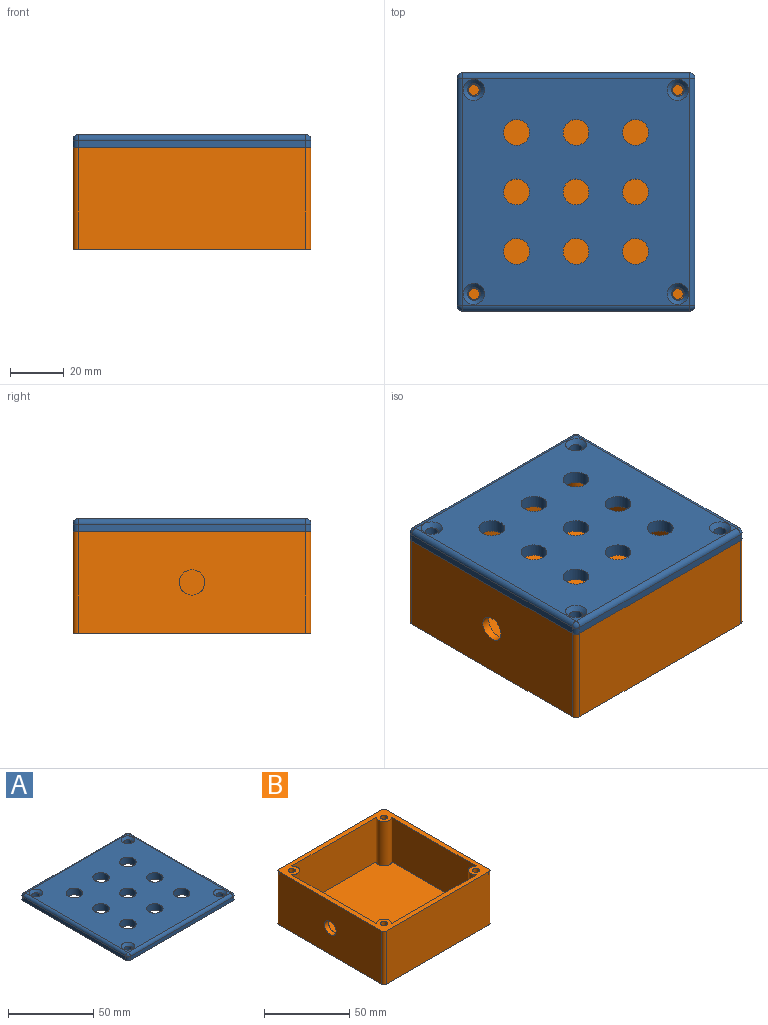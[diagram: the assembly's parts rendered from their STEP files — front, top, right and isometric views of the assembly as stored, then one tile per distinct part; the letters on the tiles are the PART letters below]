
ASSEMBLY  parts=2 mates=1
PART A: 35 faces, bbox 88.9x88.9x4.8 mm
  f0: plane 84.84x2.73mm, normal (1,0,0), area 231.6mm2, adj f18,f21,f27,f30
  f1: plane 84.84x2.73mm, normal (0,1,0), area 231.6mm2, adj f18,f24,f28,f30
  f2: plane 84.84x2.73mm, normal (-1,0,0), area 231.6mm2, adj f18,f19,f23,f24
  f3: cylinder r=2.38mm len=4.76mm, axis (0,0,-1), area 47.3mm2, adj f18,f31
  f4: cylinder r=2.38mm len=4.76mm, axis (0,0,-1), area 47.3mm2, adj f18,f33
  f5: cylinder r=2.38mm len=4.76mm, axis (0,0,-1), area 47.3mm2, adj f18,f34
  f6: cylinder r=4.83mm len=9.65mm, axis (0,0,-1), area 144.4mm2, adj f17,f18
  f7: cylinder r=4.83mm len=9.65mm, axis (0,0,-1), area 144.4mm2, adj f17,f18
  f8: cylinder r=4.83mm len=9.65mm, axis (0,0,-1), area 144.4mm2, adj f17,f18
  f9: cylinder r=4.83mm len=9.65mm, axis (0,0,-1), area 144.4mm2, adj f17,f18
  f10: cylinder r=4.83mm len=9.65mm, axis (0,0,-1), area 144.4mm2, adj f17,f18
  f11: cylinder r=4.83mm len=9.65mm, axis (0,0,-1), area 144.4mm2, adj f17,f18
  f12: cylinder r=4.83mm len=9.65mm, axis (0,0,-1), area 144.4mm2, adj f17,f18
  f13: cylinder r=4.83mm len=9.65mm, axis (0,0,-1), area 144.4mm2, adj f17,f18
  f14: cylinder r=4.83mm len=9.65mm, axis (0,0,-1), area 144.4mm2, adj f17,f18
  f15: plane 84.84x2.73mm, normal (0,-1,0), area 231.6mm2, adj f18,f19,f21,f22
  f16: cylinder r=2.38mm len=4.76mm, axis (0,0,-1), area 47.3mm2, adj f18,f32
  f17: plane 84.84x84.84mm, normal (0,0,1), area 6340.7mm2, adj f6,f7,f8,f9,f10,f11,f12,f13
  f18: plane 88.9x88.9mm, normal (0,0,-1), area 7169.9mm2, adj f0,f1,f2,f3,f4,f5,f6,f7
  f19: cylinder r=2.03mm len=2.73mm, axis (0,0,1), area 8.7mm2, adj f2,f15,f18,f20
  f20: sphere r=2.03mm, area 6.5mm2, adj f19,f22,f23
  f21: cylinder r=2.03mm len=2.73mm, axis (0,0,-1), area 8.7mm2, adj f0,f15,f18,f25
  f22: cylinder r=2.03mm len=84.84mm, axis (-1,0,0), area 270.8mm2, adj f15,f17,f20,f25
  f23: cylinder r=2.03mm len=84.84mm, axis (0,1,0), area 270.8mm2, adj f2,f17,f20,f26
  f24: cylinder r=2.03mm len=2.73mm, axis (0,0,-1), area 8.7mm2, adj f1,f2,f18,f26
  f25: sphere r=2.03mm, area 6.5mm2, adj f21,f22,f27
  f26: sphere r=2.03mm, area 6.5mm2, adj f23,f24,f28
  f27: cylinder r=2.03mm len=84.84mm, axis (0,-1,0), area 270.8mm2, adj f0,f17,f25,f29
  f28: cylinder r=2.03mm len=84.84mm, axis (1,0,0), area 270.8mm2, adj f1,f17,f26,f29
  f29: sphere r=2.03mm, area 6.5mm2, adj f27,f28,f30
  f30: cylinder r=2.03mm len=2.73mm, axis (0,0,1), area 8.7mm2, adj f0,f1,f18,f29
  f31: cone r=2.38mm half-angle=44.8deg, axis (0,0,1), area 45mm2, adj f3,f17
  f32: cone r=2.38mm half-angle=44.8deg, axis (0,0,1), area 45mm2, adj f16,f17
  f33: cone r=2.38mm half-angle=44.8deg, axis (0,0,1), area 45mm2, adj f4,f17
  f34: cone r=2.38mm half-angle=44.8deg, axis (0,0,1), area 45mm2, adj f5,f17
PART B: 28 faces, bbox 88.9x88.9x38.1 mm
  f0: plane 69.85x31.75mm, normal (0,1,0), area 2217.7mm2, adj f1,f15,f16,f18
  f1: cylinder r=4.49mm len=31.75mm, axis (0,0,-1), area 447.9mm2, adj f0,f2,f16,f18
  f2: plane 69.85x31.75mm, normal (1,0,0), area 2146.5mm2, adj f1,f3,f16,f18,f27
  f3: cylinder r=4.49mm len=31.75mm, axis (0,0,-1), area 447.9mm2, adj f2,f4,f16,f18
  f4: plane 69.85x31.75mm, normal (0,-1,0), area 2217.7mm2, adj f3,f5,f16,f18
  f5: cylinder r=4.49mm len=31.75mm, axis (0,0,-1), area 447.9mm2, adj f4,f6,f16,f18
  f6: plane 69.85x31.75mm, normal (-1,0,0), area 2217.7mm2, adj f5,f15,f16,f18
  f7: plane 84.84x38.1mm, normal (1,0,0), area 3232.3mm2, adj f16,f17,f23,f26
  f8: plane 84.84x38.1mm, normal (0,1,0), area 3232.3mm2, adj f16,f17,f23,f24
  f9: plane 84.84x38.1mm, normal (-1,0,0), area 3161mm2, adj f16,f17,f24,f25,f27
  f10: cylinder r=2.1mm len=31.75mm, axis (0,0,-1), area 418.7mm2, adj f16,f22
  f11: cylinder r=1.98mm len=31.75mm, axis (0,0,-1), area 395.9mm2, adj f16,f21
  f12: cylinder r=1.98mm len=31.75mm, axis (0,0,-1), area 395.9mm2, adj f16,f20
  f13: cylinder r=1.98mm len=31.75mm, axis (0,0,-1), area 395.9mm2, adj f16,f19
  f14: plane 84.84x38.1mm, normal (0,-1,0), area 3232.3mm2, adj f16,f17,f25,f26
  f15: cylinder r=4.49mm len=31.75mm, axis (0,0,-1), area 447.9mm2, adj f0,f6,f16,f18
  f16: plane 88.9x88.9mm, normal (0,0,1), area 1241.5mm2, adj f0,f1,f2,f3,f4,f5,f6,f7
  f17: plane 88.9x88.9mm, normal (0,0,-1), area 7899.7mm2, adj f7,f8,f9,f14,f23,f24,f25,f26
  f18: plane 82.55x82.55mm, normal (0,0,1), area 6607.2mm2, adj f0,f1,f2,f3,f4,f5,f6,f15
  f19: plane 3.97x3.97mm, normal (0,0,1), area 12.4mm2, adj f13
  f20: plane 3.97x3.97mm, normal (0,0,1), area 12.4mm2, adj f12
  f21: plane 3.97x3.97mm, normal (0,0,1), area 12.4mm2, adj f11
  f22: plane 4.2x4.2mm, normal (0,0,1), area 13.8mm2, adj f10
  f23: cylinder r=2.03mm len=38.1mm, axis (0,0,1), area 121.6mm2, adj f7,f8,f16,f17
  f24: cylinder r=2.03mm len=38.1mm, axis (0,0,-1), area 121.6mm2, adj f8,f9,f16,f17
  f25: cylinder r=2.03mm len=38.1mm, axis (0,0,1), area 121.6mm2, adj f9,f14,f16,f17
  f26: cylinder r=2.03mm len=38.1mm, axis (0,0,-1), area 121.6mm2, adj f7,f14,f16,f17
  f27: cylinder r=4.76mm len=9.53mm, axis (-1,0,0), area 95mm2, adj f2,f9
PLACE A t=(0.02,-0.35,-4.79)mm
PLACE B t=(0.02,-0.35,-42.89)mm
MATE fastened B.f26 <-> A.f21  axis (0,0,1) through (42.43,-42.77,-4.79)mm
